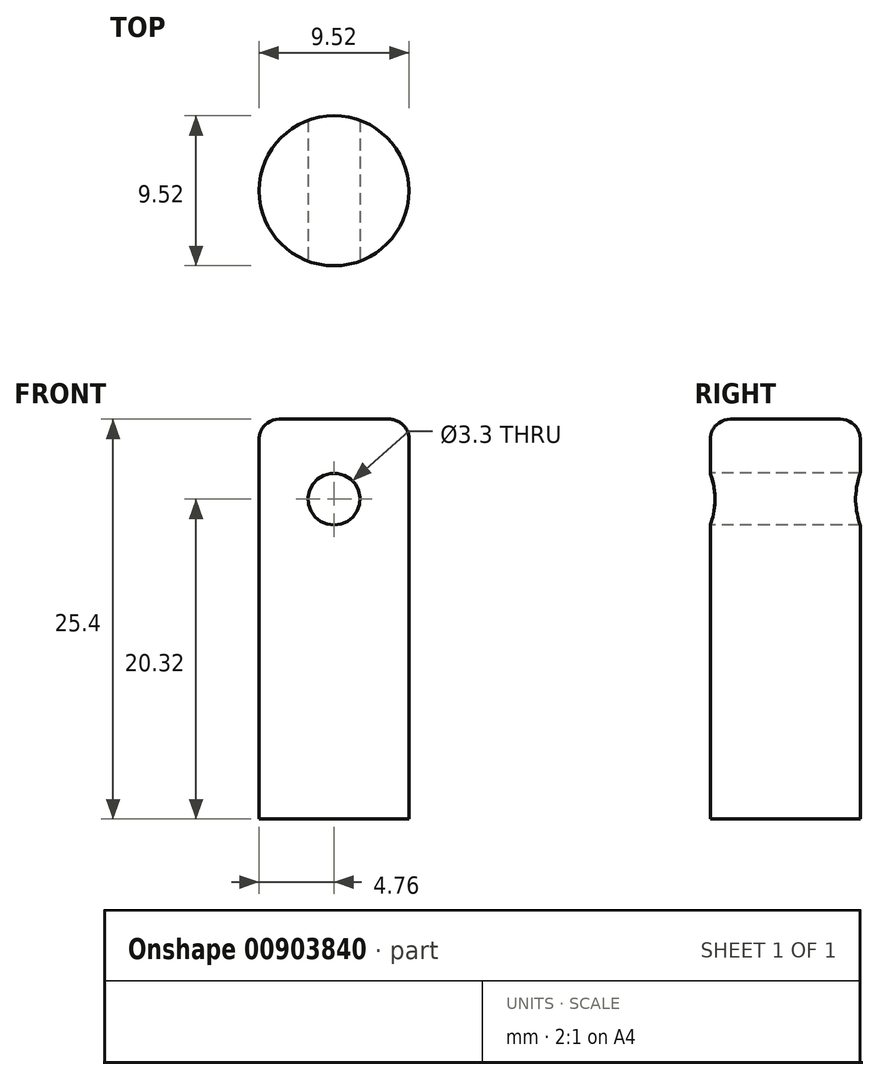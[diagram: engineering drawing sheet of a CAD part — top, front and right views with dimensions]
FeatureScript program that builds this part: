
annotation { "Feature Type Name" : "Feature", "Feature Type Description" : "" }
export const myFeature = defineFeature(function(context is Context, id is Id, definition is map)
    precondition{}
    {
        {
            var Q0;
            Q0=qCreatedBy(makeId("Top.planeOp"),FACE);
            var sketch = newSketch(context, id + "F0", { "sketchPlane" : qUnion([Q0])});
            skCircle(sketch, "E0", {"center": v(0, 0) * mm, "radius": 4.76 * mm});
            skSolve(sketch);
        }
        {
            var Q0;
            Q0=qSketchRegion(id+"F0",true);
            extrude(context, id + "F1", {"entities" : qUnion([Q0]), "oppositeDirection" : true, "depth" : 25.4 * mm, "offsetDistance" : 25.4 * mm});
        }
        {
            var Q0;
            Q0=qCreatedBy(makeId("Front.planeOp"),FACE);
            var sketch = newSketch(context, id + "F2", { "sketchPlane" : qUnion([Q0])});
            skLineSegment(sketch, "E1", {"start": v(0, 0) * mm, "end": v(0, -5.08) * mm, "construction": true});
            skCircle(sketch, "E2", {"center": v(0, -5.08) * mm, "radius": 1.65 * mm});
            skSolve(sketch);
        }
        {
            var Q0;
            Q0=qSketchRegion(id+"F2",true);
            extrude(context, id + "F3", {"entities" : qUnion([Q0]), "operationType" : NewBodyOperationType.REMOVE, "endBound" : BoundingType.THROUGH_ALL, "oppositeDirection" : true, "depth" : 25.4 * mm, "offsetDistance" : 25.4 * mm, "hasSecondDirection" : true, "secondDirectionOppositeDirection" : false, "secondDirectionDepth" : 25.4 * mm});
        }
        {
            var Q0;
            Q0=makeQuery(id+"F1.opExtrude","CAP_EDGE",EDGE,{"disambiguationData":[OSD([sQuery(id+"F0.wireOp",EDGE,"E0")])],"isStart":true});
            fillet(context, id + "F4", {"entities" : qUnion([Q0]), "radius" : 1.27 * mm, "tangentPropagation" : true, "allowEdgeOverflow" : false});
        }
    });
